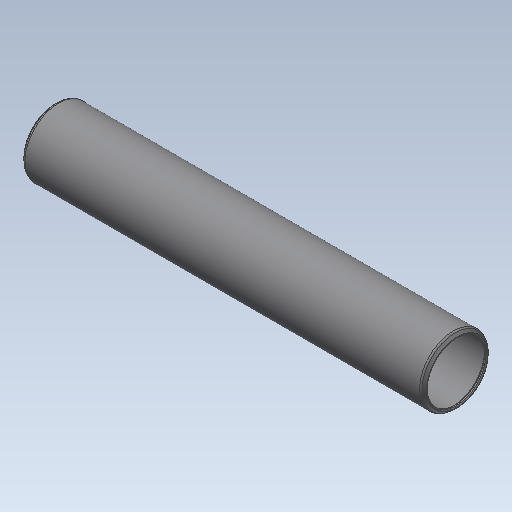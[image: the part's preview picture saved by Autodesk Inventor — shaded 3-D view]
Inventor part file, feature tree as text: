
AUTODESK INVENTOR PART (.ipt)
format: ipt  version: 2020 (Build 240168000, 168)  size: 150,528 bytes
history: native  units: in
note: dims shown in document units (in); Inventor stores cm internally (conversion verified against a paired STEP export)
features: other x42, revolve x1, sketch x1
ambient origin geometry x8: Origin, YZ Plane, XZ Plane, XY Plane, X Axis, Y Axis, Z Axis, Center Point
bodies: Solid1 (feature_tree)
feature tree (44):
  revolve  "Revolution1"  [1 undecoded]
  other  "cp1_XY"
  other  "cp1_YZ"
  other  "cp1_ZX"
  other  "cp1_X"
  other  "cp1_Y"
  other  "cp1_Z"
  other  "cp1_Center"
  other  "cp2_XY"
  other  "cp2_YZ"
  other  "cp2_ZX"
  other  "cp2_X"
  other  "cp2_Y"
  other  "cp2_Z"
  other  "cp2_Center"
  other  "cp3_XY"
  other  "cp3_YZ"
  other  "cp3_ZX"
  other  "cp3_X"
  other  "cp3_Y"
  other  "cp3_Z"
  other  "cp3_Center"
  other  "cp4_XY"
  other  "cp4_YZ"
  other  "cp4_ZX"
  other  "cp4_X"
  other  "cp4_Y"
  other  "cp4_Z"
  other  "cp4_Center"
  other  "tube_front_XY"
  other  "tube_front_YZ"
  other  "tube_front_ZX"
  other  "tube_front_X"
  other  "tube_front_Y"
  other  "tube_front_Z"
  other  "tube_front_Center"
  other  "tube_rear_XY"
  other  "tube_rear_YZ"
  other  "tube_rear_ZX"
  other  "tube_rear_X"
  other  "tube_rear_Y"
  other  "tube_rear_Z"
  other  "tube_rear_Center"
  sketch  "Sketch_1"  dims[d0=360.0deg]
note: 1 required parameter value undecoded (feature->parameter linkage not recoverable at this tier; creation-order binding heuristic only, values carry confidence <= 0.55)
